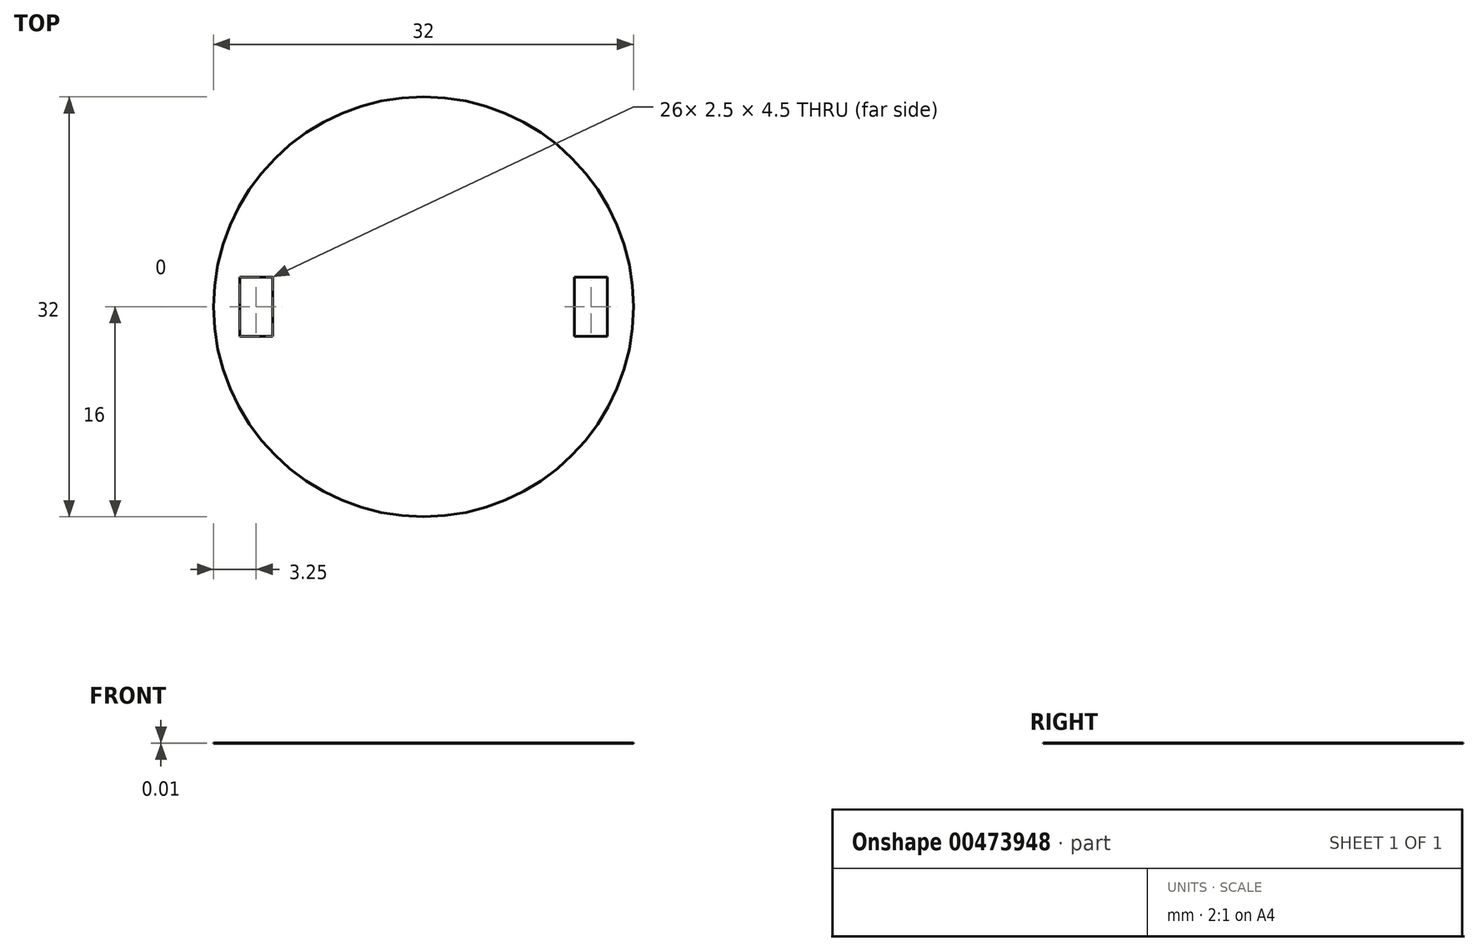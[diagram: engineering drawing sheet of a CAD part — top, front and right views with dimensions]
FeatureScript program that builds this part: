
annotation { "Feature Type Name" : "Feature", "Feature Type Description" : "" }
export const myFeature = defineFeature(function(context is Context, id is Id, definition is map)
    precondition{}
    {
        {
            var Q0;
            Q0=qCreatedBy(makeId("Top.planeOp"),FACE);
            var sketch = newSketch(context, id + "F0", { "sketchPlane" : qUnion([Q0])});
            skCircle(sketch, "E0", {"center": v(0, 0) * mm, "radius": 16 * mm});
            skLineSegment(sketch, "E1", {"start": v(0, 0) * mm, "end": v(11.5, 0) * mm, "construction": true});
            skLineSegment(sketch, "E2", {"start": v(0, 0) * mm, "end": v(-11.5, 0) * mm, "construction": true});
            skLineSegment(sketch, "E3.bottom", {"start": v(-14, 2.25) * mm, "end": v(-11.5, 2.25) * mm});
            skLineSegment(sketch, "E3.top", {"start": v(-14, -2.25) * mm, "end": v(-11.5, -2.25) * mm});
            skLineSegment(sketch, "E3.left", {"start": v(-14, 2.25) * mm, "end": v(-14, -2.25) * mm});
            skLineSegment(sketch, "E3.right", {"start": v(-11.5, 2.25) * mm, "end": v(-11.5, -2.25) * mm});
            skLineSegment(sketch, "E4", {"start": v(-14, 0) * mm, "end": v(-11.5, 0) * mm, "construction": true});
            skLineSegment(sketch, "E5.bottom", {"start": v(11.5, 2.25) * mm, "end": v(14, 2.25) * mm});
            skLineSegment(sketch, "E5.top", {"start": v(11.5, -2.25) * mm, "end": v(14, -2.25) * mm});
            skLineSegment(sketch, "E5.left", {"start": v(11.5, 2.25) * mm, "end": v(11.5, -2.25) * mm});
            skLineSegment(sketch, "E5.right", {"start": v(14, 2.25) * mm, "end": v(14, -2.25) * mm});
            skLineSegment(sketch, "E6", {"start": v(11.5, 0) * mm, "end": v(14, 0) * mm, "construction": true});
            skSolve(sketch);
        }
        {
            var Q0;
            Q0 = qSketchRegion(id + "F0", true);
            extrude(context, id + "F1", {"entities" : qUnion([Q0]), "depth" : 1 / 101.6 * mm});
        }
    });
